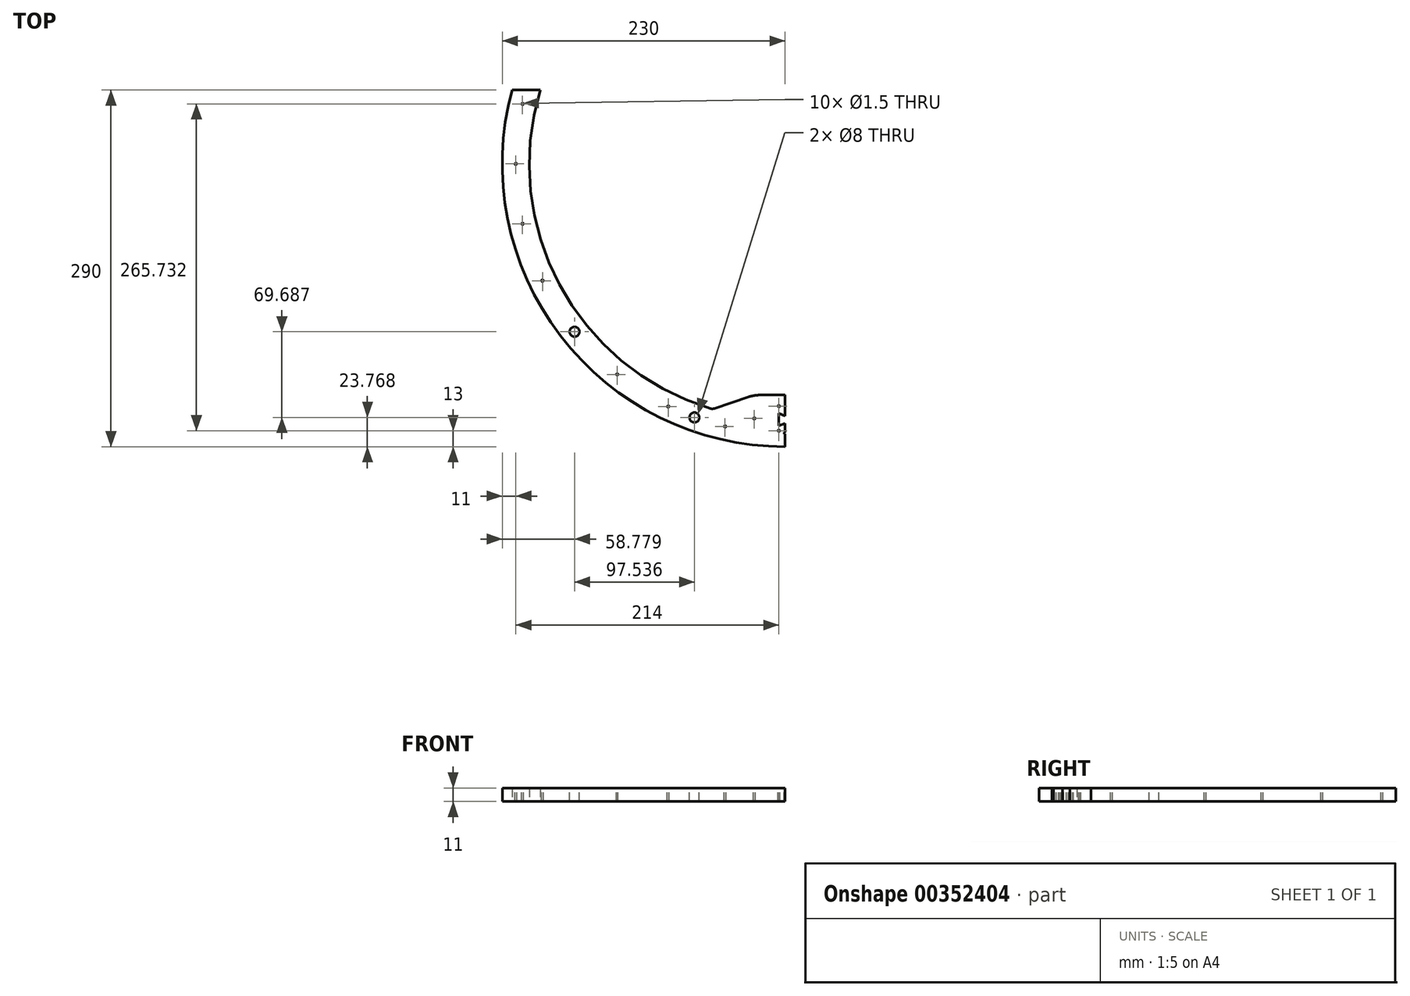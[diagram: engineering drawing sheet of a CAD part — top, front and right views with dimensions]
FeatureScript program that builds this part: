
annotation { "Feature Type Name" : "Feature", "Feature Type Description" : "" }
export const myFeature = defineFeature(function(context is Context, id is Id, definition is map)
    precondition{}
    {
        {
            var Q0;
            Q0=qCreatedBy(makeId("Top.planeOp"),FACE);
            var sketch = newSketch(context, id + "F0", { "sketchPlane" : qUnion([Q0])});
            skArc(sketch, "E0", {"start": v(-199.16, 60) * mm, "mid": v(-183.03, -98.8) * mm, "end": v(-59.12, -199.42) * mm});
            skArc(sketch, "E1", {"start": v(-222.04, 60) * mm, "mid": v(0, -230) * mm, "end": v(222.04, 60) * mm});
            skLineSegment(sketch, "E2", {"start": v(0, 0) * mm, "end": v(-114.72, 0) * mm, "construction": true});
            skLineSegment(sketch, "E3", {"start": v(0, 0) * mm, "end": v(0, 60) * mm, "construction": true});
            skLineSegment(sketch, "E4", {"start": v(199.16, 60) * mm, "end": v(222.04, 60) * mm});
            skLineSegment(sketch, "E5.MirrorCS", {"start": v(-199.16, 60) * mm, "end": v(-222.04, 60) * mm});
            skLineSegment(sketch, "E6", {"start": v(0, -208) * mm, "end": v(0, -188) * mm, "construction": true});
            skLineSegment(sketch, "E7", {"start": v(0, -188) * mm, "end": v(25, -188) * mm});
            skLineSegment(sketch, "E8", {"start": v(25, -188) * mm, "end": v(59.12, -199.42) * mm});
            skLineSegment(sketch, "E9.MirrorCS", {"start": v(0, -188) * mm, "end": v(-25, -188) * mm});
            skLineSegment(sketch, "E10.MirrorCS", {"start": v(-25, -188) * mm, "end": v(-59.12, -199.42) * mm});
            skArc(sketch, "E11.trimOffspring", {"start": v(59.12, -199.42) * mm, "mid": v(183.03, -98.8) * mm, "end": v(199.16, 60) * mm});
            skPoint(sketch, "E12.orphan", {"position": v(0, 60) * mm});
            skSolve(sketch);
        }
        {
            var Q0;
            Q0=qSketchRegion(id+"F0",true);
            extrude(context, id + "F1", {"entities" : qUnion([Q0]), "depth" : 11 * mm});
        }
        {
            var Q0;
            Q0=makeQuery(id+"F1.opExtrude","SWEPT_EDGE",EDGE,{"disambiguationData":[OSD([sQuery(id+"F0.wireOp",EDGE,"E7"),sQuery(id+"F0.wireOp",EDGE,"E8")])]});
            var Q1;
            Q1=makeQuery(id+"F1.opExtrude","SWEPT_EDGE",EDGE,{"disambiguationData":[OSD([sQuery(id+"F0.wireOp",EDGE,"E9.MirrorCS"),sQuery(id+"F0.wireOp",EDGE,"E10.MirrorCS")])]});
            fillet(context, id + "F2", {"entities" : qUnion([Q0, Q1]), "radius" : 28.52 * mm, "tangentPropagation" : true, "allowEdgeOverflow" : false});
        }
        {
            var Q0;
            Q0=makeQuery(id+"F1.opExtrude","SWEPT_EDGE",EDGE,{"disambiguationData":[OSD([sQuery(id+"F0.wireOp",EDGE,"E8"),sQuery(id+"F0.wireOp",EDGE,"E11.trimOffspring")])]});
            var Q1;
            Q1=makeQuery(id+"F1.opExtrude","SWEPT_EDGE",EDGE,{"disambiguationData":[OSD([sQuery(id+"F0.wireOp",EDGE,"E0"),sQuery(id+"F0.wireOp",EDGE,"E10.MirrorCS")])]});
            fillet(context, id + "F3", {"entities" : qUnion([Q0, Q1]), "radius" : 5 * mm, "tangentPropagation" : true, "allowEdgeOverflow" : false});
        }
        {
            var Q0;
            Q0=qCreatedBy(makeId("Top.planeOp"),FACE);
            var sketch = newSketch(context, id + "F4", { "sketchPlane" : qUnion([Q0])});
            skLineSegment(sketch, "E13", {"start": v(0, 0) * mm, "end": v(174.2, -171.38) * mm, "construction": true});
            skLineSegment(sketch, "E14", {"start": v(0, 0) * mm, "end": v(0, 36.6) * mm, "construction": true});
            skLineSegment(sketch, "E15.MirrorCS", {"start": v(0, 0) * mm, "end": v(-174.2, -171.38) * mm, "construction": true});
            skSolve(sketch);
        }
        {
            var Q0;
            Q0=makeQuery(id+"F1.opExtrude","CAP_FACE",FACE,{"disambiguationData":[OSD([sQuery(id+"F0.wireOp",EDGE,"E0"),sQuery(id+"F0.wireOp",EDGE,"E1"),sQuery(id+"F0.wireOp",EDGE,"E4"),sQuery(id+"F0.wireOp",EDGE,"E5.MirrorCS"),sQuery(id+"F0.wireOp",EDGE,"E7"),sQuery(id+"F0.wireOp",EDGE,"E8"),sQuery(id+"F0.wireOp",EDGE,"E9.MirrorCS"),sQuery(id+"F0.wireOp",EDGE,"E10.MirrorCS"),sQuery(id+"F0.wireOp",EDGE,"E11.trimOffspring")])],"isStart":false});
            var sketch = newSketch(context, id + "F5", { "sketchPlane" : qUnion([Q0])});
            skArc(sketch, "E16.0", {"start": v(-217.44, 26.07) * mm, "mid": v(0, -219) * mm, "end": v(217.44, 26.07) * mm, "construction": true});
            skCircle(sketch, "E17", {"center": v(0, -219) * mm, "radius": 0.75 * mm});
            skCircle(sketch, "E18.1.0", {"center": v(48.73, -213.5) * mm, "radius": 0.75 * mm});
            skCircle(sketch, "E18.2.0", {"center": v(95.02, -197.31) * mm, "radius": 0.75 * mm});
            skCircle(sketch, "E18.3.0", {"center": v(136.54, -171.22) * mm, "radius": 0.75 * mm});
            skCircle(sketch, "E18.4.0", {"center": v(171.22, -136.54) * mm, "radius": 0.75 * mm});
            skCircle(sketch, "E18.5.0", {"center": v(197.31, -95.02) * mm, "radius": 0.75 * mm});
            skCircle(sketch, "E18.6.0", {"center": v(213.5, -48.73) * mm, "radius": 0.75 * mm});
            skCircle(sketch, "E18.7.0", {"center": v(219, 0) * mm, "radius": 0.75 * mm});
            skCircle(sketch, "E18.8.0", {"center": v(213.5, 48.73) * mm, "radius": 0.75 * mm});
            skCircle(sketch, "E18.9.0", {"center": v(197.31, 95.02) * mm, "radius": 0.75 * mm});
            skCircle(sketch, "E18.10.0", {"center": v(171.22, 136.54) * mm, "radius": 0.75 * mm});
            skCircle(sketch, "E18.11.0", {"center": v(136.54, 171.22) * mm, "radius": 0.75 * mm});
            skCircle(sketch, "E18.12.0", {"center": v(95.02, 197.31) * mm, "radius": 0.75 * mm});
            skCircle(sketch, "E18.13.0", {"center": v(48.73, 213.5) * mm, "radius": 0.75 * mm});
            skCircle(sketch, "E18.14.0", {"center": v(0, 219) * mm, "radius": 0.75 * mm});
            skCircle(sketch, "E18.15.0", {"center": v(-48.73, 213.5) * mm, "radius": 0.75 * mm});
            skCircle(sketch, "E18.16.0", {"center": v(-95.02, 197.31) * mm, "radius": 0.75 * mm});
            skCircle(sketch, "E18.17.0", {"center": v(-136.54, 171.22) * mm, "radius": 0.75 * mm});
            skCircle(sketch, "E18.18.0", {"center": v(-171.22, 136.54) * mm, "radius": 0.75 * mm});
            skCircle(sketch, "E18.19.0", {"center": v(-197.31, 95.02) * mm, "radius": 0.75 * mm});
            skCircle(sketch, "E18.20.0", {"center": v(-213.5, 48.73) * mm, "radius": 0.75 * mm});
            skCircle(sketch, "E18.21.0", {"center": v(-219, 0) * mm, "radius": 0.75 * mm});
            skCircle(sketch, "E18.22.0", {"center": v(-213.5, -48.73) * mm, "radius": 0.75 * mm});
            skCircle(sketch, "E18.23.0", {"center": v(-197.31, -95.02) * mm, "radius": 0.75 * mm});
            skCircle(sketch, "E18.24.0", {"center": v(-171.22, -136.54) * mm, "radius": 0.75 * mm});
            skCircle(sketch, "E18.25.0", {"center": v(-136.54, -171.22) * mm, "radius": 0.75 * mm});
            skCircle(sketch, "E18.26.0", {"center": v(-95.02, -197.31) * mm, "radius": 0.75 * mm});
            skCircle(sketch, "E18.27.0", {"center": v(-48.73, -213.5) * mm, "radius": 0.75 * mm});
            skCircle(sketch, "E19", {"center": v(-5, -197) * mm, "radius": 0.75 * mm});
            skLineSegment(sketch, "E20", {"start": v(0, 0) * mm, "end": v(0, -93.12) * mm, "construction": true});
            skLineSegment(sketch, "E21", {"start": v(0, -219) * mm, "end": v(0, -197) * mm, "construction": true});
            skLineSegment(sketch, "E22", {"start": v(0, -197) * mm, "end": v(-5, -197) * mm, "construction": true});
            skCircle(sketch, "E23.MirrorC", {"center": v(5, -197) * mm, "radius": 0.75 * mm});
            skLineSegment(sketch, "E24", {"start": v(-5, -197) * mm, "end": v(-5, -217) * mm, "construction": true});
            skPoint(sketch, "E25.endSnap0", {"position": v(-5, -207) * mm});
            skLineSegment(sketch, "E26", {"start": v(-5, -207) * mm, "end": v(-25, -207) * mm, "construction": true});
            skCircle(sketch, "E27", {"center": v(0, -208) * mm, "radius": 0.75 * mm});
            skCircle(sketch, "E28.MirrorC", {"center": v(-5, -217) * mm, "radius": 0.75 * mm});
            skCircle(sketch, "E29", {"center": v(-25, -207) * mm, "radius": 0.75 * mm});
            skCircle(sketch, "E30.MirrorC", {"center": v(5, -217) * mm, "radius": 0.75 * mm});
            skCircle(sketch, "E31.MirrorC", {"center": v(25, -207) * mm, "radius": 0.75 * mm});
            skCircle(sketch, "E32", {"center": v(-73.68, -206.23) * mm, "radius": 4 * mm});
            skSolve(sketch);
        }
        {
            var Q0;
            Q0=qSketchRegion(id+"F5",true);
            extrude(context, id + "F6", {"entities" : qUnion([Q0]), "operationType" : NewBodyOperationType.REMOVE, "endBound" : BoundingType.THROUGH_ALL, "oppositeDirection" : true, "depth" : 25 * mm});
        }
        {
            var Q0;
            Q0=makeQuery(id+"F1.opExtrude","CAP_FACE",FACE,{"disambiguationData":[OSD([sQuery(id+"F0.wireOp",EDGE,"E0"),sQuery(id+"F0.wireOp",EDGE,"E1"),sQuery(id+"F0.wireOp",EDGE,"E4"),sQuery(id+"F0.wireOp",EDGE,"E5.MirrorCS"),sQuery(id+"F0.wireOp",EDGE,"E7"),sQuery(id+"F0.wireOp",EDGE,"E8"),sQuery(id+"F0.wireOp",EDGE,"E9.MirrorCS"),sQuery(id+"F0.wireOp",EDGE,"E10.MirrorCS"),sQuery(id+"F0.wireOp",EDGE,"E11.trimOffspring")])],"isStart":false});
            var sketch = newSketch(context, id + "F7", { "sketchPlane" : qUnion([Q0])});
            skCircle(sketch, "E33", {"center": v(-171.22, -136.54) * mm, "radius": 4 * mm});
            skLineSegment(sketch, "E34", {"start": v(0, 0) * mm, "end": v(0, -100.25) * mm, "construction": true});
            skCircle(sketch, "E35.MirrorC", {"center": v(171.22, -136.54) * mm, "radius": 4 * mm});
            skSolve(sketch);
        }
        {
            var Q0;
            Q0=qSketchRegion(id+"F7",true);
            extrude(context, id + "F8", {"entities" : qUnion([Q0]), "operationType" : NewBodyOperationType.REMOVE, "endBound" : BoundingType.THROUGH_ALL, "oppositeDirection" : true, "depth" : 25 * mm});
        }
        {
            var Q0;
            Q0=makeQuery(id+"F1.opExtrude","CAP_FACE",FACE,{"disambiguationData":[OSD([sQuery(id+"F0.wireOp",EDGE,"E0"),sQuery(id+"F0.wireOp",EDGE,"E1"),sQuery(id+"F0.wireOp",EDGE,"E4"),sQuery(id+"F0.wireOp",EDGE,"E5.MirrorCS"),sQuery(id+"F0.wireOp",EDGE,"E7"),sQuery(id+"F0.wireOp",EDGE,"E8"),sQuery(id+"F0.wireOp",EDGE,"E9.MirrorCS"),sQuery(id+"F0.wireOp",EDGE,"E10.MirrorCS"),sQuery(id+"F0.wireOp",EDGE,"E11.trimOffspring")])],"isStart":false});
            var sketch = newSketch(context, id + "F9", { "sketchPlane" : qUnion([Q0])});
            skLineSegment(sketch, "E36", {"start": v(0, -188) * mm, "end": v(0, 85.64) * mm});
            skLineSegment(sketch, "E37", {"start": v(263.79, 85.64) * mm, "end": v(0, 85.64) * mm});
            skLineSegment(sketch, "E38", {"start": v(263.79, 85.64) * mm, "end": v(263.79, -251.47) * mm});
            skLineSegment(sketch, "E39", {"start": v(0, -251.47) * mm, "end": v(263.79, -251.47) * mm});
            skPoint(sketch, "E39.endSnap0", {"position": v(0, -230) * mm});
            skLineSegment(sketch, "E40", {"start": v(0, -188) * mm, "end": v(0, -205) * mm});
            skLineSegment(sketch, "E41", {"start": v(0, -211) * mm, "end": v(0, -251.47) * mm});
            skLineSegment(sketch, "E42", {"start": v(0, -208) * mm, "end": v(0, -205) * mm, "construction": true});
            skLineSegment(sketch, "E43", {"start": v(0, -208) * mm, "end": v(0, -211) * mm, "construction": true});
            skLineSegment(sketch, "E44", {"start": v(0, -205) * mm, "end": v(-5, -202.92) * mm});
            skLineSegment(sketch, "E45", {"start": v(0, -208) * mm, "end": v(7.63, -208) * mm, "construction": true});
            skLineSegment(sketch, "E46.MirrorCS", {"start": v(0, -211) * mm, "end": v(-5, -213.08) * mm});
            skLineSegment(sketch, "E47", {"start": v(-5, -202.92) * mm, "end": v(-5, -213.08) * mm});
            skSolve(sketch);
        }
        {
            var Q0;
            Q0=qSketchRegion(id+"F9",true);
            extrude(context, id + "F10", {"entities" : qUnion([Q0]), "operationType" : NewBodyOperationType.REMOVE, "endBound" : BoundingType.THROUGH_ALL, "oppositeDirection" : true, "depth" : 25 * mm});
        }
    });
